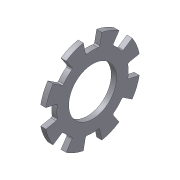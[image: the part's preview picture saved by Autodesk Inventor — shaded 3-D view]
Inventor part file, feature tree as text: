
AUTODESK INVENTOR PART (.ipt)
format: ipt  version: 2011 (Build 150239000, 239)  size: 128,512 bytes
history: native  units: mm (DEFAULTED — no unit token found)
features: extrude x1, pattern_circular x1
ambient origin geometry x8: Origin, YZ Plane, XZ Plane, XY Plane, X Axis, Y Axis, Z Axis, Center Point
bodies: Solid1 (feature_tree), Body (feature_tree)
feature tree (2):
  extrude  "Cut"  Depth=12.954mm
  pattern_circular  "Cuts"  [2 undecoded]
note: 2 required parameter values undecoded (feature->parameter linkage not recoverable at this tier; creation-order binding heuristic only, values carry confidence <= 0.55)
